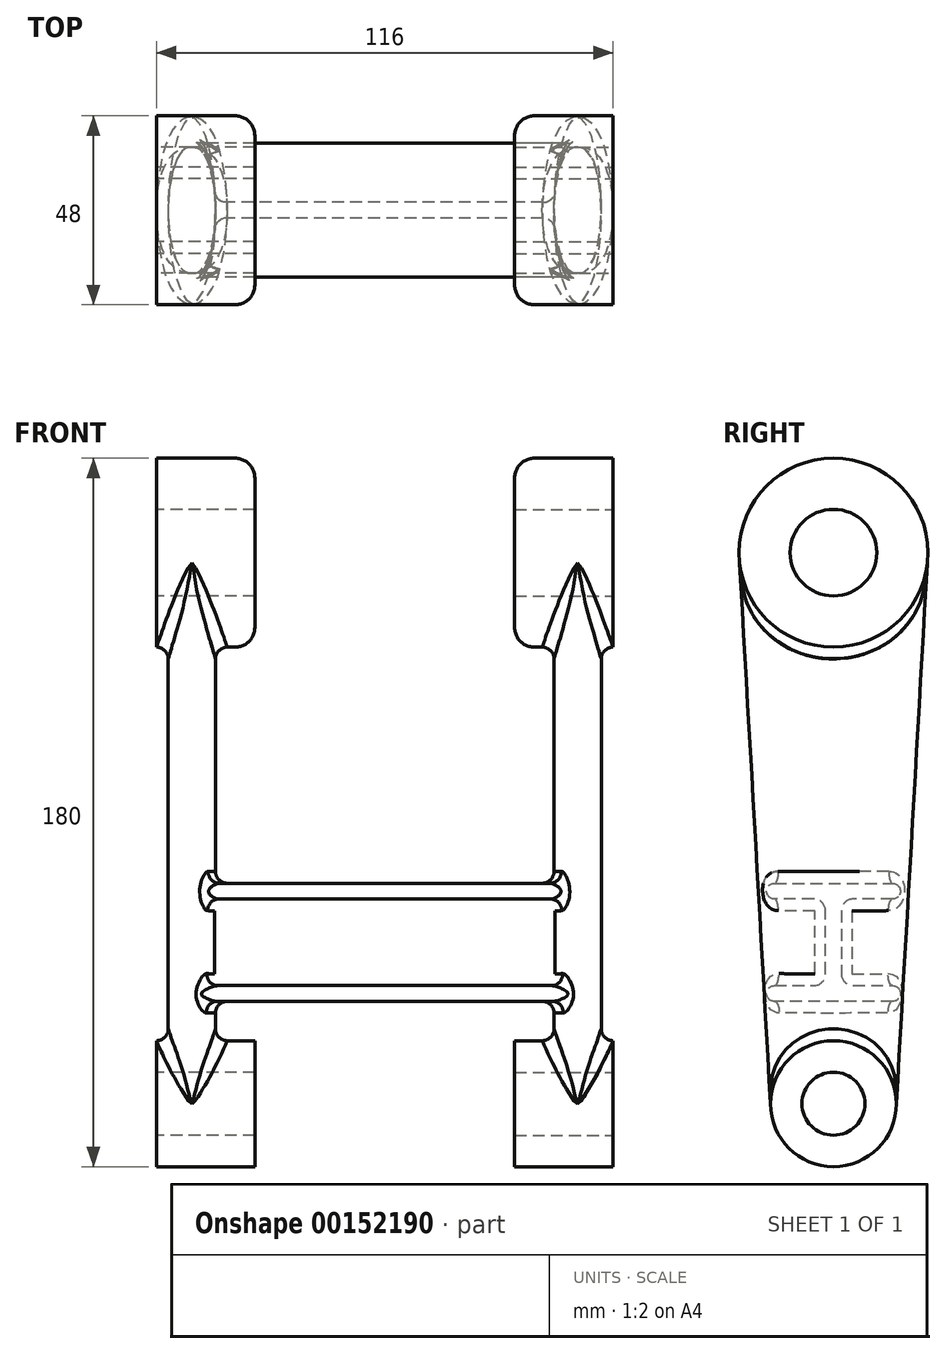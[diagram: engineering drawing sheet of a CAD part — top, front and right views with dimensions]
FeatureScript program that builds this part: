
annotation { "Feature Type Name" : "Feature", "Feature Type Description" : "" }
export const myFeature = defineFeature(function(context is Context, id is Id, definition is map)
    precondition{}
    {
        {
            var Q0;
            Q0=qCreatedBy(makeId("Right.planeOp"),FACE);
            var sketch = newSketch(context, id + "F0", { "sketchPlane" : qUnion([Q0])});
            skCircle(sketch, "E0", {"center": v(0, 0) * mm, "radius": 16 * mm});
            skCircle(sketch, "E1", {"center": v(0, 0) * mm, "radius": 8 * mm});
            skCircle(sketch, "E2", {"center": v(0, 140) * mm, "radius": 24 * mm});
            skCircle(sketch, "E3", {"center": v(0, 140) * mm, "radius": 11 * mm});
            skSolve(sketch);
        }
        {
            var Q0;
            Q0=makeQuery(id+"F0.imprint","IMPRINT",FACE,{"disambiguationData":[TD([[makeQuery(id+"F0.imprint","IMPRINT",EDGE,{"derivedFrom":sQuery(id+"F0.wireOp",EDGE,"E2")}),1.0]])]});
            var Q1;
            Q1=makeQuery(id+"F0.imprint","IMPRINT",FACE,{"disambiguationData":[TD([[makeQuery(id+"F0.imprint","IMPRINT",EDGE,{"derivedFrom":sQuery(id+"F0.wireOp",EDGE,"E3")}),1.0]])]});
            extrude(context, id + "F1", {"entities" : qUnion([Q0, Q1]), "depth" : 25 * mm});
        }
        {
            var Q0;
            Q0=makeQuery(id+"F0.imprint","IMPRINT",FACE,{"disambiguationData":[TD([[makeQuery(id+"F0.imprint","IMPRINT",EDGE,{"derivedFrom":sQuery(id+"F0.wireOp",EDGE,"E0")}),1.0]])]});
            var Q1;
            Q1=makeQuery(id+"F0.imprint","IMPRINT",FACE,{"disambiguationData":[TD([[makeQuery(id+"F0.imprint","IMPRINT",EDGE,{"derivedFrom":sQuery(id+"F0.wireOp",EDGE,"E1")}),1.0]])]});
            extrude(context, id + "F2", {"entities" : qUnion([Q0, Q1]), "depth" : 25 * mm});
        }
        {
            var Q0;
            Q0=qCreatedBy(makeId("Top.planeOp"),FACE);
            var sketch = newSketch(context, id + "F3", { "sketchPlane" : qUnion([Q0])});
            skEllipse(sketch, "E4", {"center": v(9, 0) * mm, "majorRadius": 16 * mm, "minorRadius": 6 * mm, "majorAxis": v(0, -1)});
            skLineSegment(sketch, "E5", {"start": v(0, 16) * mm, "end": v(24.3, 16) * mm, "construction": true});
            skPoint(sketch, "E6", {"position": v(3, 0) * mm});
            skSolve(sketch);
        }
        {
            var Q0;
            Q0=qCreatedBy(makeId("Top.planeOp"),FACE);
            var Q1;
            Q1=sQuery(id+"F0.wireOp",VERTEX,"E3.center");
            cPlane(context, id + "F4", {"entities" : qUnion([Q0, Q1]), "cplaneType" : CPlaneType.PLANE_POINT, "offset" : 25 * mm, "width" : 150 * mm, "height" : 150 * mm});
        }
        {
            var Q0;
            Q0=qCreatedBy(id+"F4.planeOp",FACE);
            var sketch = newSketch(context, id + "F5", { "sketchPlane" : qUnion([Q0])});
            skEllipse(sketch, "E7", {"center": v(9, 0) * mm, "majorRadius": 24 * mm, "minorRadius": 6 * mm, "majorAxis": v(0, -1)});
            skPoint(sketch, "E8", {"position": v(3, 0) * mm});
            skLineSegment(sketch, "E9", {"start": v(0, 24) * mm, "end": v(24.27, 24) * mm, "construction": true});
            skSolve(sketch);
        }
        {
            var Q0;
            Q0=qSketchRegion(id+"F5",true);
            var Q1;
            Q1=qSketchRegion(id+"F3",true);
            loft(context, id + "F6", {"operationType" : NewBodyOperationType.ADD, "sheetProfilesArray" : [{ "sheetProfileEntities" : qUnion([Q0]) }, { "sheetProfileEntities" : qUnion([Q1]) }]});
        }
        {
            var Q0;
            Q0=makeQuery(id+"F0.imprint","IMPRINT",FACE,{"disambiguationData":[TD([[makeQuery(id+"F0.imprint","IMPRINT",EDGE,{"derivedFrom":sQuery(id+"F0.wireOp",EDGE,"E3")}),1.0]])]});
            extrude(context, id + "F7", {"entities" : qUnion([Q0]), "operationType" : NewBodyOperationType.REMOVE, "endBound" : BoundingType.THROUGH_ALL, "depth" : 25 * mm});
        }
        {
            var Q0;
            Q0=makeQuery(id+"F0.imprint","IMPRINT",FACE,{"disambiguationData":[TD([[makeQuery(id+"F0.imprint","IMPRINT",EDGE,{"derivedFrom":sQuery(id+"F0.wireOp",EDGE,"E1")}),1.0]])]});
            extrude(context, id + "F8", {"entities" : qUnion([Q0]), "operationType" : NewBodyOperationType.REMOVE, "endBound" : BoundingType.THROUGH_ALL, "depth" : 25 * mm});
        }
        {
            var Q0;
            Q0=qCreatedBy(makeId("Right.planeOp"),FACE);
            cPlane(context, id + "F9", {"entities" : qUnion([Q0]), "cplaneType" : CPlaneType.OFFSET, "offset" : 8 * mm, "width" : 150 * mm, "height" : 150 * mm});
        }
        {
            var Q0;
            Q0=qCreatedBy(id+"F9.planeOp",FACE);
            var sketch = newSketch(context, id + "F10", { "sketchPlane" : qUnion([Q0])});
            skLineSegment(sketch, "E10", {"start": v(-15, 52) * mm, "end": v(-5, 52) * mm});
            skLineSegment(sketch, "E11", {"start": v(-2, 49) * mm, "end": v(-2, 33) * mm});
            skLineSegment(sketch, "E12", {"start": v(-5, 30) * mm, "end": v(-15, 30) * mm});
            skLineSegment(sketch, "E13", {"start": v(-15, 26) * mm, "end": v(15, 26) * mm});
            skLineSegment(sketch, "E14", {"start": v(15, 30) * mm, "end": v(5, 30) * mm});
            skLineSegment(sketch, "E15", {"start": v(2, 33) * mm, "end": v(2, 49) * mm});
            skLineSegment(sketch, "E16", {"start": v(5, 52) * mm, "end": v(15, 52) * mm});
            skLineSegment(sketch, "E17", {"start": v(15, 56) * mm, "end": v(-15, 56) * mm});
            skPoint(sketch, "E18.visualSharp", {"position": v(2, 52) * mm});
            skArc(sketch, "E18.filletArc", {"start": v(5, 52) * mm, "mid": v(2.88, 51.12) * mm, "end": v(2, 49) * mm});
            skPoint(sketch, "E19.visualSharp", {"position": v(-2, 52) * mm});
            skArc(sketch, "E19.filletArc", {"start": v(-2, 49) * mm, "mid": v(-2.88, 51.12) * mm, "end": v(-5, 52) * mm});
            skPoint(sketch, "E20.visualSharp", {"position": v(-2, 30) * mm});
            skArc(sketch, "E20.filletArc", {"start": v(-5, 30) * mm, "mid": v(-2.88, 30.88) * mm, "end": v(-2, 33) * mm});
            skPoint(sketch, "E21.visualSharp", {"position": v(2, 30) * mm});
            skArc(sketch, "E21.filletArc", {"start": v(2, 33) * mm, "mid": v(2.88, 30.88) * mm, "end": v(5, 30) * mm});
            skArc(sketch, "E22", {"start": v(15, 52) * mm, "mid": v(17, 54) * mm, "end": v(15, 56) * mm});
            skArc(sketch, "E23", {"start": v(-15, 56) * mm, "mid": v(-17, 54) * mm, "end": v(-15, 52) * mm});
            skArc(sketch, "E24", {"start": v(-15, 30) * mm, "mid": v(-17, 28) * mm, "end": v(-15, 26) * mm});
            skArc(sketch, "E25", {"start": v(15, 26) * mm, "mid": v(17, 28) * mm, "end": v(15, 30) * mm});
            skPoint(sketch, "E26", {"position": v(0, 56) * mm});
            skPoint(sketch, "E27", {"position": v(0, 26) * mm});
            skLineSegment(sketch, "E28", {"start": v(16, 0) * mm, "end": v(24, 140) * mm, "construction": true});
            skSolve(sketch);
        }
        {
            var Q0;
            Q0=qSketchRegion(id+"F10",true);
            extrude(context, id + "F11", {"entities" : qUnion([Q0]), "operationType" : NewBodyOperationType.ADD, "depth" : 52 * mm});
        }
        {
            var Q0;
            Q0=qCreatedBy(makeId("Right.planeOp"),FACE);
            cPlane(context, id + "F12", {"entities" : qUnion([Q0]), "cplaneType" : CPlaneType.OFFSET, "offset" : 58 * mm, "width" : 150 * mm, "height" : 150 * mm});
        }
        {
            var Q0;
            Q0=makeQuery(id+"F1.opExtrude","SWEPT_BODY",BODY,{"disambiguationData":[OSD([sQuery(id+"F0.wireOp",EDGE,"E2")])]});
            var Q1;
            Q1=qCreatedBy(id+"F12.planeOp",FACE);
            mirror(context, id + "F13", {"operationType" : NewBodyOperationType.ADD, "entities" : qUnion([Q0]), "mirrorPlane" : qUnion([Q1])});
        }
        {
            var Q0;
            Q0=makeQuery(id+"F11.boolean.opBoolean","INTERSECT",EDGE,{"derivedFrom":[makeQuery(id+"F6.opLoft","SWEPT_FACE",FACE,{"disambiguationData":[OSD([sQuery(id+"F3.wireOp",EDGE,"E4"),sQuery(id+"F5.wireOp",EDGE,"E7")])]}),makeQuery(id+"F11.opExtrude","SWEPT_FACE",FACE,{"disambiguationData":[OSD([sQuery(id+"F10.wireOp",EDGE,"E17")])]})]});
            var Q1;
            Q1=makeQuery(id+"F11.boolean.opBoolean","INTERSECT",EDGE,{"derivedFrom":[makeQuery(id+"F6.opLoft","SWEPT_FACE",FACE,{"disambiguationData":[OSD([sQuery(id+"F3.wireOp",EDGE,"E4"),sQuery(id+"F5.wireOp",EDGE,"E7")])]}),makeQuery(id+"F11.opExtrude","SWEPT_FACE",FACE,{"disambiguationData":[OSD([sQuery(id+"F10.wireOp",EDGE,"E23")])]})]});
            var Q2;
            Q2=makeQuery(id+"F6.boolean.opBoolean","INTERSECT",EDGE,{"derivedFrom":[makeQuery(id+"F2.opExtrude","SWEPT_FACE",FACE,{"disambiguationData":[OSD([sQuery(id+"F0.wireOp",EDGE,"E0")])]}),makeQuery(id+"F6.opLoft","SWEPT_FACE",FACE,{"disambiguationData":[OSD([sQuery(id+"F3.wireOp",EDGE,"E4"),sQuery(id+"F5.wireOp",EDGE,"E7")])]})]});
            var Q3;
            Q3=makeQuery(id+"F6.boolean.opBoolean","INTERSECT",EDGE,{"derivedFrom":[makeQuery(id+"F1.opExtrude","SWEPT_FACE",FACE,{"disambiguationData":[OSD([sQuery(id+"F0.wireOp",EDGE,"E2")])]}),makeQuery(id+"F6.opLoft","SWEPT_FACE",FACE,{"disambiguationData":[OSD([sQuery(id+"F3.wireOp",EDGE,"E4"),sQuery(id+"F5.wireOp",EDGE,"E7")])]})]});
            var Q4;
            Q4=makeQuery(id+"F6.opLoft","SWEPT_FACE",FACE,{"disambiguationData":[OSD([sQuery(id+"F3.wireOp",EDGE,"E4"),sQuery(id+"F5.wireOp",EDGE,"E7")])]});
            var Q5;
            Q5=makeQuery(id+"F13.opPattern","COPY",EDGE,{"derivedFrom":makeQuery(id+"F6.boolean.opBoolean","INTERSECT",EDGE,{"derivedFrom":[makeQuery(id+"F1.opExtrude","SWEPT_FACE",FACE,{"disambiguationData":[OSD([sQuery(id+"F0.wireOp",EDGE,"E2")])]}),makeQuery(id+"F6.opLoft","SWEPT_FACE",FACE,{"disambiguationData":[OSD([sQuery(id+"F3.wireOp",EDGE,"E4"),sQuery(id+"F5.wireOp",EDGE,"E7")])]})]}),"instanceName":"1"});
            var Q6;
            Q6=makeQuery(id+"F13.opPattern","COPY",EDGE,{"derivedFrom":makeQuery(id+"F6.boolean.opBoolean","INTERSECT",EDGE,{"derivedFrom":[makeQuery(id+"F2.opExtrude","SWEPT_FACE",FACE,{"disambiguationData":[OSD([sQuery(id+"F0.wireOp",EDGE,"E0")])]}),makeQuery(id+"F6.opLoft","SWEPT_FACE",FACE,{"disambiguationData":[OSD([sQuery(id+"F3.wireOp",EDGE,"E4"),sQuery(id+"F5.wireOp",EDGE,"E7")])]})]}),"instanceName":"1"});
            var Q7;
            Q7=makeQuery(id+"F13.opPattern","COPY",EDGE,{"derivedFrom":makeQuery(id+"F11.boolean.opBoolean","INTERSECT",EDGE,{"derivedFrom":[makeQuery(id+"F6.opLoft","SWEPT_FACE",FACE,{"disambiguationData":[OSD([sQuery(id+"F3.wireOp",EDGE,"E4"),sQuery(id+"F5.wireOp",EDGE,"E7")])]}),makeQuery(id+"F11.opExtrude","SWEPT_FACE",FACE,{"disambiguationData":[OSD([sQuery(id+"F10.wireOp",EDGE,"E11")])]})]}),"instanceName":"1"});
            fillet(context, id + "F14", {"entities" : qUnion([Q0, Q1, Q2, Q3, Q4, Q5, Q6, Q7]), "radius" : 3 * mm, "tangentPropagation" : true, "allowEdgeOverflow" : false});
        }
        {
            var Q0;
            Q0=makeQuery(id+"F13.opPattern","COPY",EDGE,{"derivedFrom":makeQuery(id+"F1.opExtrude","CAP_EDGE",EDGE,{"disambiguationData":[OSD([sQuery(id+"F0.wireOp",EDGE,"E2")])],"isStart":false}),"instanceName":"1"});
            var Q1;
            Q1=makeQuery(id+"F1.opExtrude","CAP_EDGE",EDGE,{"disambiguationData":[OSD([sQuery(id+"F0.wireOp",EDGE,"E2")])],"isStart":false});
            fillet(context, id + "F15", {"entities" : qUnion([Q0, Q1]), "radius" : 5 * mm, "tangentPropagation" : true, "allowEdgeOverflow" : false});
        }
    });
